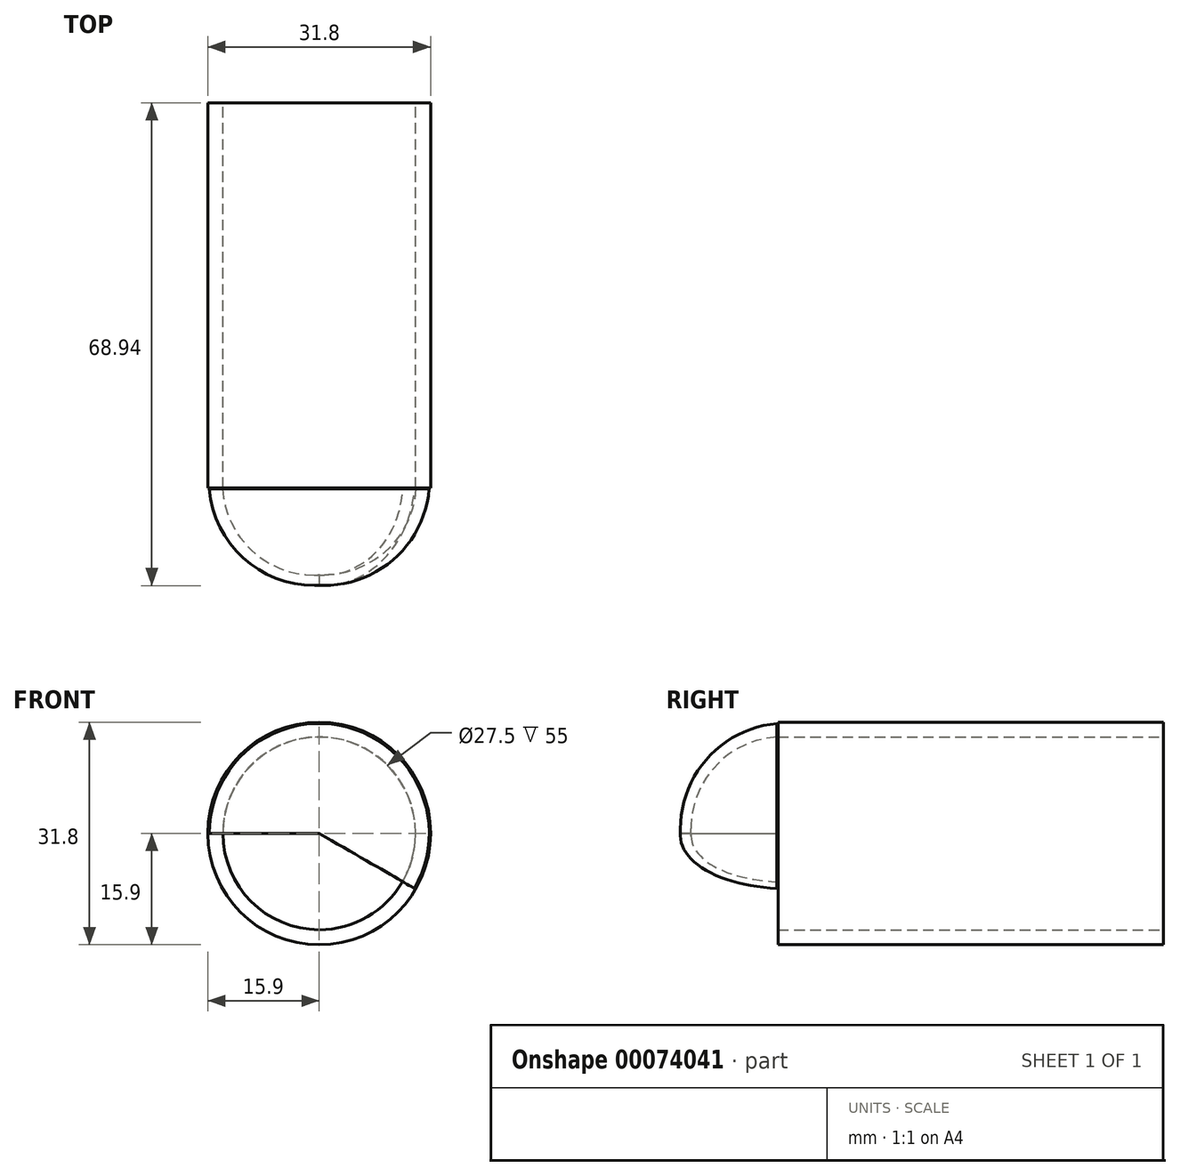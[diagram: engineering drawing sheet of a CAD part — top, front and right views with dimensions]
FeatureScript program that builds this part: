
annotation { "Feature Type Name" : "Feature", "Feature Type Description" : "" }
export const myFeature = defineFeature(function(context is Context, id is Id, definition is map)
    precondition{}
    {
        {
            var Q0;
            Q0=qCreatedBy(makeId("Front.planeOp"),FACE);
            var sketch = newSketch(context, id + "F0", { "sketchPlane" : qUnion([Q0])});
            skCircle(sketch, "E0", {"center": v(0, 0) * mm, "radius": 13.75 * mm});
            skCircle(sketch, "E1", {"center": v(0, 0) * mm, "radius": 15.9 * mm});
            skSolve(sketch);
        }
        {
            var Q0;
            Q0=makeQuery(id+"F0.imprint","IMPRINT",FACE,{"disambiguationData":[TD([[makeQuery(id+"F0.imprint","IMPRINT",EDGE,{"derivedFrom":sQuery(id+"F0.wireOp",EDGE,"E0")}),-1.0]])]});
            extrude(context, id + "F1", {"entities" : qUnion([Q0]), "depth" : 55 * mm});
        }
        {
            var Q0;
            Q0=qCreatedBy(makeId("Top.planeOp"),FACE);
            var sketch = newSketch(context, id + "F2", { "sketchPlane" : qUnion([Q0])});
            skArc(sketch, "E2", {"start": v(0, -68.92) * mm, "mid": v(10.62, -65.2) * mm, "end": v(15.7, -55.15) * mm});
            skArc(sketch, "E3", {"start": v(0, -67.4) * mm, "mid": v(9.43, -64.11) * mm, "end": v(13.78, -55.12) * mm});
            skLineSegment(sketch, "E4", {"start": v(13.78, -55.12) * mm, "end": v(15.7, -55.15) * mm});
            skLineSegment(sketch, "E5", {"start": v(0, -67.4) * mm, "end": v(0, -68.92) * mm});
            skSolve(sketch);
        }
        {
            var Q0;
            Q0=makeQuery(id+"F2.imprint","IMPRINT",FACE,{"disambiguationData":[TD([[makeQuery(id+"F2.imprint","IMPRINT",EDGE,{"derivedFrom":sQuery(id+"F2.wireOp",EDGE,"E2")}),1.0]])]});
            var Q1;
            Q1=sQuery(id+"F2.wireOp",EDGE,"E5");
            revolve(context, id + "F3", {"entities" : qUnion([Q0]), "axis" : qUnion([Q1]), "revolveType" : RevolveType.TWO_DIRECTIONS, "angle" : 180 * degree, "angleBack" : 330 * degree});
        }
    });
